# Revit family: 1326xxx - KOS Concrete Round (GU10)
name_source: partatom
category: Lighting Fixtures
revit_build: Autodesk Revit 2018 (Build: 20170223_1515(x64)
units: mm (PartAtom-declared; Revit-internal decimal feet)

## family parameters
Always vertical = Yes
Cut with Voids When Loaded = No
Host = Ceiling
Light Source = No
OmniClass Number = 23.80.70.11
OmniClass Title = Luminaries for Internal Lighting
Part Type = Normal
Room Calculation Point = No
Round Connector Dimension = Use Diameter
Shared = No

## types (1)
- Astro Kos Round Concrete
    Dimmable = Lamp Dependent
    Dimming Method = Lamp Dependent
    Efficacy (lm/w) = Lamp Dependent
    Electrical Class = Class 1
    Lamp = GU 10
    Light Source Fixed = No
    Location / IP Rating = IP 44
    Main Finish = Matt Concrete
    Main Material = Concrete
    Manufacturer URL - Europe and Rest of World = www.astrolighting.com
    Manufacturer URL - North America = us.astrolighting.com
    Power (Watts) = 6 W LED Max
    Product CCT = Lamp Dependent
    Product CRI = Lamp Dependent
    Product Dimensions (MM) = 141 H x 110 Dia
    Product Location = Outdoor/Indoor/Bathroom/Coastal, Zone 1,2,3
    Product Name = Kos Round
    Product SKU = 1326014
    Product URL = https://www.astrolighting.com
    Product Weight (KG) = 1 mm  [stored 0.00328084 ft]
    Wattage Comments = -

note: [stored X ft] marks values corroborated as IEEE doubles in the binary element streams (Revit-internal decimal feet)

## geometry (parser evidence)
native form markers: Sweep x2
no freeform markers — native parametric forms only
